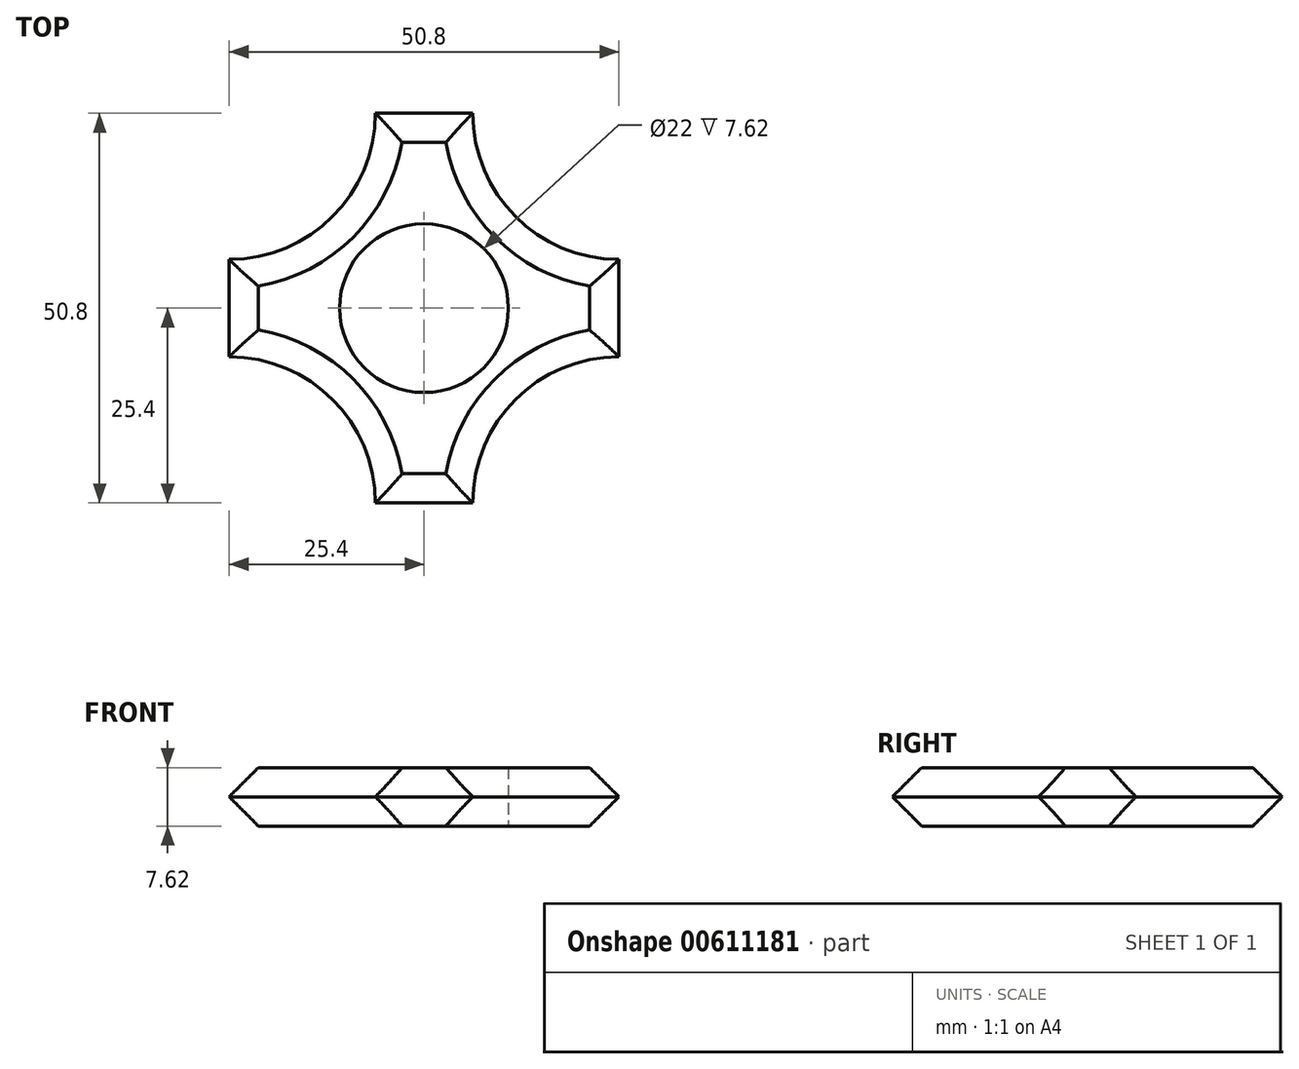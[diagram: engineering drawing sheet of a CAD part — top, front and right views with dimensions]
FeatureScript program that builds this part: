
annotation { "Feature Type Name" : "Feature", "Feature Type Description" : "" }
export const myFeature = defineFeature(function(context is Context, id is Id, definition is map)
    precondition{}
    {
        {
            var Q0;
            Q0=qCreatedBy(makeId("Top.planeOp"),FACE);
            var sketch = newSketch(context, id + "F0", { "sketchPlane" : qUnion([Q0])});
            skPoint(sketch, "E0.middle", {"position": v(0, 0) * mm});
            skCircle(sketch, "E1", {"center": v(0, 0) * mm, "radius": 11 * mm});
            skLineSegment(sketch, "E2.bottom", {"start": v(25.4, 25.4) * mm, "end": v(-25.4, 25.4) * mm});
            skLineSegment(sketch, "E2.top", {"start": v(25.4, -25.4) * mm, "end": v(-25.4, -25.4) * mm});
            skLineSegment(sketch, "E2.left", {"start": v(25.4, 25.4) * mm, "end": v(25.4, -25.4) * mm});
            skLineSegment(sketch, "E2.right", {"start": v(-25.4, 25.4) * mm, "end": v(-25.4, -25.4) * mm});
            skCircle(sketch, "E3", {"center": v(25.4, 25.4) * mm, "radius": 19.05 * mm});
            skCircle(sketch, "E4", {"center": v(25.4, -25.4) * mm, "radius": 19.05 * mm});
            skCircle(sketch, "E5.MirrorC", {"center": v(-25.4, 25.4) * mm, "radius": 19.05 * mm});
            skCircle(sketch, "E6.MirrorC", {"center": v(-25.4, -25.4) * mm, "radius": 19.05 * mm});
            skSolve(sketch);
        }
        {
            var Q0;
            Q0=makeQuery(id+"F0.imprint","IMPRINT",FACE,{"disambiguationData":[TD([[makeQuery(id+"F0.imprint","IMPRINT",EDGE,{"derivedFrom":sQuery(id+"F0.wireOp",EDGE,"E1")}),-1.0]])]});
            extrude(context, id + "F1", {"entities" : qUnion([Q0]), "depth" : 7.62 * mm, "offsetDistance" : 25.4 * mm});
        }
        {
            var Q0;
            Q0=makeQuery(id+"F1.opExtrude","CAP_EDGE",EDGE,{"disambiguationData":[OSD([sQuery(id+"F0.wireOp",EDGE,"E3")])],"isStart":false});
            var Q1;
            Q1=makeQuery(id+"F1.opExtrude","CAP_EDGE",EDGE,{"disambiguationData":[OSD([sQuery(id+"F0.wireOp",EDGE,"E5.MirrorC")])],"isStart":false});
            var Q2;
            Q2=makeQuery(id+"F1.opExtrude","CAP_EDGE",EDGE,{"disambiguationData":[OSD([sQuery(id+"F0.wireOp",EDGE,"E2.bottom")])],"isStart":false});
            var Q3;
            Q3=makeQuery(id+"F1.opExtrude","CAP_EDGE",EDGE,{"disambiguationData":[OSD([sQuery(id+"F0.wireOp",EDGE,"E2.left")])],"isStart":false});
            var Q4;
            Q4=makeQuery(id+"F1.opExtrude","CAP_EDGE",EDGE,{"disambiguationData":[OSD([sQuery(id+"F0.wireOp",EDGE,"E4")])],"isStart":false});
            var Q5;
            Q5=makeQuery(id+"F1.opExtrude","CAP_EDGE",EDGE,{"disambiguationData":[OSD([sQuery(id+"F0.wireOp",EDGE,"E2.top")])],"isStart":false});
            var Q6;
            Q6=makeQuery(id+"F1.opExtrude","CAP_EDGE",EDGE,{"disambiguationData":[OSD([sQuery(id+"F0.wireOp",EDGE,"E6.MirrorC")])],"isStart":false});
            var Q7;
            Q7=makeQuery(id+"F1.opExtrude","CAP_EDGE",EDGE,{"disambiguationData":[OSD([sQuery(id+"F0.wireOp",EDGE,"E2.right")])],"isStart":false});
            var Q8;
            Q8=makeQuery(id+"F1.opExtrude","CAP_EDGE",EDGE,{"disambiguationData":[OSD([sQuery(id+"F0.wireOp",EDGE,"E5.MirrorC")])],"isStart":true});
            var Q9;
            Q9=makeQuery(id+"F1.opExtrude","CAP_EDGE",EDGE,{"disambiguationData":[OSD([sQuery(id+"F0.wireOp",EDGE,"E2.bottom")])],"isStart":true});
            var Q10;
            Q10=makeQuery(id+"F1.opExtrude","CAP_EDGE",EDGE,{"disambiguationData":[OSD([sQuery(id+"F0.wireOp",EDGE,"E3")])],"isStart":true});
            var Q11;
            Q11=makeQuery(id+"F1.opExtrude","CAP_EDGE",EDGE,{"disambiguationData":[OSD([sQuery(id+"F0.wireOp",EDGE,"E4")])],"isStart":true});
            var Q12;
            Q12=makeQuery(id+"F1.opExtrude","CAP_EDGE",EDGE,{"disambiguationData":[OSD([sQuery(id+"F0.wireOp",EDGE,"E2.left")])],"isStart":true});
            var Q13;
            Q13=makeQuery(id+"F1.opExtrude","CAP_EDGE",EDGE,{"disambiguationData":[OSD([sQuery(id+"F0.wireOp",EDGE,"E6.MirrorC")])],"isStart":true});
            var Q14;
            Q14=makeQuery(id+"F1.opExtrude","CAP_EDGE",EDGE,{"disambiguationData":[OSD([sQuery(id+"F0.wireOp",EDGE,"E2.top")])],"isStart":true});
            var Q15;
            Q15=makeQuery(id+"F1.opExtrude","CAP_EDGE",EDGE,{"disambiguationData":[OSD([sQuery(id+"F0.wireOp",EDGE,"E2.right")])],"isStart":true});
            chamfer(context, id + "F2", {"entities" : qUnion([Q0, Q1, Q2, Q3, Q4, Q5, Q6, Q7, Q8, Q9, Q10, Q11, Q12, Q13, Q14, Q15]), "width" : 3.8 * mm, "tangentPropagation" : true});
        }
    });
